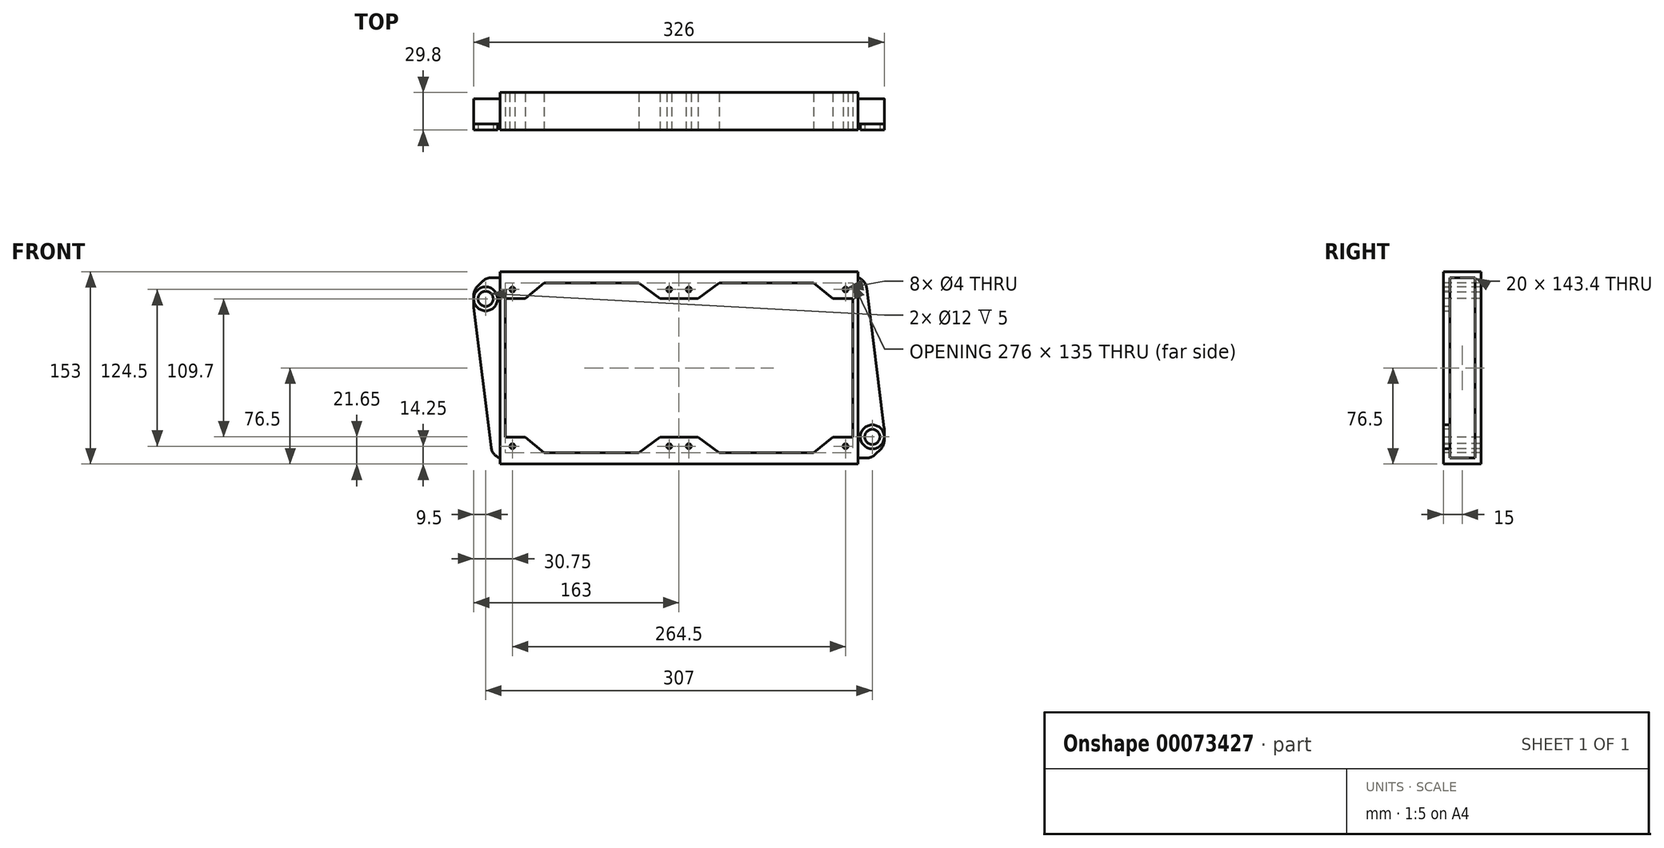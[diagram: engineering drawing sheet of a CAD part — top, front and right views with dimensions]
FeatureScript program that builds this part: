
annotation { "Feature Type Name" : "Feature", "Feature Type Description" : "" }
export const myFeature = defineFeature(function(context is Context, id is Id, definition is map)
    precondition{}
    {
        {
            var Q0;
            Q0=qCreatedBy(makeId("Front.planeOp"),FACE);
            var sketch = newSketch(context, id + "F0", { "sketchPlane" : qUnion([Q0])});
            skLineSegment(sketch, "E0.bottom", {"start": v(0, 71.7) * mm, "end": v(326, 71.7) * mm});
            skLineSegment(sketch, "E0.top", {"start": v(0, -71.7) * mm, "end": v(326, -71.7) * mm});
            skLineSegment(sketch, "E0.left", {"start": v(0, 71.7) * mm, "end": v(0, -71.7) * mm});
            skLineSegment(sketch, "E0.right", {"start": v(326, 71.7) * mm, "end": v(326, -71.7) * mm});
            skPoint(sketch, "E1", {"position": v(0, 0) * mm});
            skSolve(sketch);
        }
        {
            var Q0;
            Q0=qSketchRegion(id+"F0",true);
            extrude(context, id + "F1", {"entities" : qUnion([Q0]), "depth" : 20 * mm});
        }
        {
            var Q0;
            Q0=makeQuery(id+"F1.opExtrude","CAP_FACE",FACE,{"disambiguationData":[OSD([sQuery(id+"F0.wireOp",EDGE,"E0.bottom"),sQuery(id+"F0.wireOp",EDGE,"E0.top"),sQuery(id+"F0.wireOp",EDGE,"E0.left"),sQuery(id+"F0.wireOp",EDGE,"E0.right")])],"isStart":false});
            var sketch = newSketch(context, id + "F2", { "sketchPlane" : qUnion([Q0])});
            skCircle(sketch, "E2", {"center": v(9.5, 54.85) * mm, "radius": 9.5 * mm});
            skCircle(sketch, "E3", {"center": v(316.5, -54.85) * mm, "radius": 9.5 * mm});
            skLineSegment(sketch, "E4", {"start": v(326, 0) * mm, "end": v(0, 0) * mm, "construction": true});
            skSolve(sketch);
        }
        {
            var Q0;
            Q0=qSketchRegion(id+"F2",true);
            extrude(context, id + "F3", {"entities" : qUnion([Q0]), "operationType" : NewBodyOperationType.ADD, "depth" : 5 * mm});
        }
        {
            var Q0;
            Q0=makeQuery(id+"F3.opExtrude","CAP_FACE",FACE,{"disambiguationData":[OSD([sQuery(id+"F2.wireOp",EDGE,"E2")])],"isStart":false});
            var sketch = newSketch(context, id + "F4", { "sketchPlane" : qUnion([Q0])});
            skCircle(sketch, "E5", {"center": v(9.5, 54.85) * mm, "radius": 6 * mm});
            skCircle(sketch, "E6", {"center": v(316.5, -54.85) * mm, "radius": 6 * mm});
            skSolve(sketch);
        }
        {
            var Q0;
            Q0=qSketchRegion(id+"F4",true);
            extrude(context, id + "F5", {"entities" : qUnion([Q0]), "operationType" : NewBodyOperationType.REMOVE, "oppositeDirection" : true, "depth" : 5 * mm});
        }
        {
            var Q0;
            Q0=makeQuery(id+"F1.opExtrude","SWEPT_FACE",FACE,{"disambiguationData":[OSD([sQuery(id+"F0.wireOp",EDGE,"E0.left")])]});
            cPlane(context, id + "F6", {"entities" : qUnion([Q0]), "cplaneType" : CPlaneType.OFFSET, "offset" : 21 * mm, "oppositeDirection" : true, "width" : 150 * mm, "height" : 150 * mm});
        }
        {
            var Q0;
            Q0=qCreatedBy(id+"F6.planeOp",FACE);
            var sketch = newSketch(context, id + "F7", { "sketchPlane" : qUnion([Q0])});
            skLineSegment(sketch, "E7.bottom", {"start": v(-4.8, 76.5) * mm, "end": v(24.8, 76.5) * mm});
            skLineSegment(sketch, "E7.top", {"start": v(-4.8, -76.5) * mm, "end": v(24.8, -76.5) * mm});
            skLineSegment(sketch, "E7.left", {"start": v(-4.8, 76.5) * mm, "end": v(-4.8, -76.5) * mm});
            skLineSegment(sketch, "E7.right", {"start": v(24.8, 76.5) * mm, "end": v(24.8, -76.5) * mm});
            skLineSegment(sketch, "E8", {"start": v(0, 0) * mm, "end": v(-4.8, 0) * mm, "construction": true});
            skLineSegment(sketch, "E9.bottom", {"start": v(0, 71.7) * mm, "end": v(20, 71.7) * mm});
            skLineSegment(sketch, "E9.top", {"start": v(0, -71.7) * mm, "end": v(20, -71.7) * mm});
            skLineSegment(sketch, "E9.left", {"start": v(0, 71.7) * mm, "end": v(0, -71.7) * mm});
            skLineSegment(sketch, "E9.right", {"start": v(20, 71.7) * mm, "end": v(20, -71.7) * mm});
            skSolve(sketch);
        }
        {
            var Q0;
            Q0=qSketchRegion(id+"F7",true);
            extrude(context, id + "F8", {"entities" : qUnion([Q0]), "oppositeDirection" : true, "depth" : 284 * mm});
        }
        {
            var Q0;
            Q0=makeQuery(id+"F8.opExtrude","SWEPT_FACE",FACE,{"disambiguationData":[OSD([sQuery(id+"F7.wireOp",EDGE,"E7.right")])]});
            var sketch = newSketch(context, id + "F9", { "sketchPlane" : qUnion([Q0])});
            skCircle(sketch, "E10", {"center": v(30.75, 62.25) * mm, "radius": 2 * mm});
            skCircle(sketch, "E11", {"center": v(155.25, 62.25) * mm, "radius": 2 * mm});
            skCircle(sketch, "E12", {"center": v(170.75, 62.25) * mm, "radius": 2 * mm});
            skCircle(sketch, "E13", {"center": v(295.25, 62.25) * mm, "radius": 2 * mm});
            skLineSegment(sketch, "E14", {"start": v(21, 0) * mm, "end": v(305, 0) * mm, "construction": true});
            skLineSegment(sketch, "E15", {"start": v(163, 76.5) * mm, "end": v(163, -76.5) * mm, "construction": true});
            skCircle(sketch, "E16.MirrorC", {"center": v(30.75, -62.25) * mm, "radius": 2 * mm});
            skCircle(sketch, "E17.MirrorC", {"center": v(155.25, -62.25) * mm, "radius": 2 * mm});
            skCircle(sketch, "E18.MirrorC", {"center": v(170.75, -62.25) * mm, "radius": 2 * mm});
            skCircle(sketch, "E19.MirrorC", {"center": v(295.25, -62.25) * mm, "radius": 2 * mm});
            skSolve(sketch);
        }
        {
            var Q0;
            Q0=qSketchRegion(id+"F9",true);
            extrude(context, id + "F10", {"entities" : qUnion([Q0]), "operationType" : NewBodyOperationType.REMOVE, "endBound" : BoundingType.THROUGH_ALL, "oppositeDirection" : true, "depth" : 25 * mm});
        }
        {
            var Q0;
            Q0=makeQuery(id+"F8.opExtrude","SWEPT_FACE",FACE,{"disambiguationData":[OSD([sQuery(id+"F7.wireOp",EDGE,"E7.right")])]});
            var sketch = newSketch(context, id + "F11", { "sketchPlane" : qUnion([Q0])});
            skLineSegment(sketch, "E20", {"start": v(21, 55) * mm, "end": v(25, 55) * mm, "construction": true});
            skLineSegment(sketch, "E21", {"start": v(41, 55) * mm, "end": v(56, 67.5) * mm});
            skLineSegment(sketch, "E22", {"start": v(56, 67.5) * mm, "end": v(131, 67.5) * mm});
            skLineSegment(sketch, "E23", {"start": v(131, 67.5) * mm, "end": v(148, 55) * mm});
            skLineSegment(sketch, "E24", {"start": v(148, 55) * mm, "end": v(178, 55) * mm});
            skLineSegment(sketch, "E25", {"start": v(178, 55) * mm, "end": v(195, 67.5) * mm});
            skLineSegment(sketch, "E26", {"start": v(195, 67.5) * mm, "end": v(270, 67.5) * mm});
            skLineSegment(sketch, "E27", {"start": v(270, 67.5) * mm, "end": v(285, 55) * mm});
            skLineSegment(sketch, "E28", {"start": v(285, 55) * mm, "end": v(301, 55) * mm});
            skLineSegment(sketch, "E29", {"start": v(305, 55) * mm, "end": v(305, 0) * mm, "construction": true});
            skLineSegment(sketch, "E30", {"start": v(21, 55) * mm, "end": v(21, 0) * mm, "construction": true});
            skLineSegment(sketch, "E31", {"start": v(21, 0) * mm, "end": v(305, 0) * mm, "construction": true});
            skLineSegment(sketch, "E32", {"start": v(163, 76.5) * mm, "end": v(163, 55) * mm, "construction": true});
            skLineSegment(sketch, "E33.MirrorCS", {"start": v(305, -55) * mm, "end": v(305, 0) * mm, "construction": true});
            skLineSegment(sketch, "E34.MirrorCS", {"start": v(285, -55) * mm, "end": v(301, -55) * mm});
            skLineSegment(sketch, "E35.MirrorCS", {"start": v(270, -67.5) * mm, "end": v(285, -55) * mm});
            skLineSegment(sketch, "E36.MirrorCS", {"start": v(195, -67.5) * mm, "end": v(270, -67.5) * mm});
            skLineSegment(sketch, "E37.MirrorCS", {"start": v(178, -55) * mm, "end": v(195, -67.5) * mm});
            skLineSegment(sketch, "E38.MirrorCS", {"start": v(148, -55) * mm, "end": v(178, -55) * mm});
            skLineSegment(sketch, "E39.MirrorCS", {"start": v(131, -67.5) * mm, "end": v(148, -55) * mm});
            skLineSegment(sketch, "E40.MirrorCS", {"start": v(56, -67.5) * mm, "end": v(131, -67.5) * mm});
            skLineSegment(sketch, "E41.MirrorCS", {"start": v(41, -55) * mm, "end": v(56, -67.5) * mm});
            skLineSegment(sketch, "E42.MirrorCS", {"start": v(21, -55) * mm, "end": v(21, 0) * mm, "construction": true});
            skLineSegment(sketch, "E43.MirrorCS", {"start": v(21, -55) * mm, "end": v(25, -55) * mm, "construction": true});
            skLineSegment(sketch, "E44", {"start": v(25, 55) * mm, "end": v(25, -55) * mm});
            skLineSegment(sketch, "E45", {"start": v(301, 55) * mm, "end": v(301, -55) * mm});
            skLineSegment(sketch, "E46", {"start": v(301, 55) * mm, "end": v(305, 55) * mm, "construction": true});
            skLineSegment(sketch, "E47", {"start": v(301, -55) * mm, "end": v(305, -55) * mm, "construction": true});
            skLineSegment(sketch, "E48", {"start": v(25, -55) * mm, "end": v(41, -55) * mm});
            skLineSegment(sketch, "E49", {"start": v(25, 55) * mm, "end": v(41, 55) * mm});
            skSolve(sketch);
        }
        {
            var Q0;
            Q0=qSketchRegion(id+"F11",true);
            extrude(context, id + "F12", {"entities" : qUnion([Q0]), "operationType" : NewBodyOperationType.REMOVE, "endBound" : BoundingType.THROUGH_ALL, "oppositeDirection" : true, "depth" : 25 * mm});
        }
        {
            var Q0;
            Q0=makeQuery(id+"F1.opExtrude","SWEPT_BODY",BODY,{"disambiguationData":[OSD([sQuery(id+"F0.wireOp",EDGE,"E0.bottom"),sQuery(id+"F0.wireOp",EDGE,"E0.top"),sQuery(id+"F0.wireOp",EDGE,"E0.left"),sQuery(id+"F0.wireOp",EDGE,"E0.right")])]});
            var Q1;
            Q1=makeQuery(id+"F8.opExtrude","SWEPT_BODY",BODY,{"disambiguationData":[OSD([sQuery(id+"F7.wireOp",EDGE,"E7.bottom"),sQuery(id+"F7.wireOp",EDGE,"E7.top"),sQuery(id+"F7.wireOp",EDGE,"E7.left"),sQuery(id+"F7.wireOp",EDGE,"E7.right"),sQuery(id+"F7.wireOp",EDGE,"E9.bottom"),sQuery(id+"F7.wireOp",EDGE,"E9.top"),sQuery(id+"F7.wireOp",EDGE,"E9.left"),sQuery(id+"F7.wireOp",EDGE,"E9.right")])]});
            var Q2;
            Q2=makeQuery(id+"F8.opExtrude","SWEPT_BODY",BODY,{"disambiguationData":[OSD([sQuery(id+"F7.wireOp",EDGE,"E7.bottom"),sQuery(id+"F7.wireOp",EDGE,"E7.top"),sQuery(id+"F7.wireOp",EDGE,"E7.left"),sQuery(id+"F7.wireOp",EDGE,"E7.right"),sQuery(id+"F7.wireOp",EDGE,"E9.bottom"),sQuery(id+"F7.wireOp",EDGE,"E9.top"),sQuery(id+"F7.wireOp",EDGE,"E9.left"),sQuery(id+"F7.wireOp",EDGE,"E9.right")])]});
            booleanBodies(context, id + "F13", {"operationType" : BooleanOperationType.UNION, "tools" : qUnion([Q0, Q1, Q2])});
        }
        {
            var Q0;
            Q0=makeQuery(id+"F1.opExtrude","SWEPT_EDGE",EDGE,{"disambiguationData":[OSD([sQuery(id+"F0.wireOp",EDGE,"E0.top"),sQuery(id+"F0.wireOp",EDGE,"E0.left")])]});
            var Q1;
            Q1=makeQuery(id+"F1.opExtrude","SWEPT_EDGE",EDGE,{"disambiguationData":[OSD([sQuery(id+"F0.wireOp",EDGE,"E0.bottom"),sQuery(id+"F0.wireOp",EDGE,"E0.right")])]});
            chamfer(context, id + "F14", {"entities" : qUnion([Q0, Q1]), "chamferType" : ChamferType.TWO_OFFSETS, "width1" : 15 * mm, "oppositeDirection" : false, "width2" : 120 * mm, "tangentPropagation" : true});
        }
        {
            var Q0;
            Q0=makeQuery(id+"F1.opExtrude","SWEPT_EDGE",EDGE,{"disambiguationData":[OSD([sQuery(id+"F0.wireOp",EDGE,"E0.bottom"),sQuery(id+"F0.wireOp",EDGE,"E0.left")])]});
            var Q1;
            Q1=makeQuery(id+"F1.opExtrude","SWEPT_EDGE",EDGE,{"disambiguationData":[OSD([sQuery(id+"F0.wireOp",EDGE,"E0.top"),sQuery(id+"F0.wireOp",EDGE,"E0.right")])]});
            chamfer(context, id + "F15", {"entities" : qUnion([Q0, Q1]), "width" : 10 * mm, "tangentPropagation" : true});
        }
        {
            var Q0;
            {var subQ1=sQuery(id+"F0.wireOp",EDGE,"E0.left");var subQ3=sQuery(id+"F0.wireOp",EDGE,"E0.bottom");Q0=makeQuery(id+"F15.opChamfer","BLEND_EDGE",EDGE,{"blendedFrom":[makeQuery(id+"F1.opExtrude","SWEPT_EDGE",EDGE,{"disambiguationData":[OSD([subQ3,subQ1])]}),makeQuery(id+"F13.opBoolean","SPLIT",FACE,{"disambiguationData":[TD([makeQuery(id+"F1.opExtrude","SWEPT_FACE",FACE,{"disambiguationData":[OSD([subQ1])]})])],"derivedFrom":makeQuery(id+"F1.opExtrude","SWEPT_FACE",FACE,{"disambiguationData":[OSD([subQ3])]})})],"blendedInto":[makeQuery(id+"F13.opBoolean","SPLIT",FACE,{"disambiguationData":[TD([makeQuery(id+"F1.opExtrude","SWEPT_FACE",FACE,{"disambiguationData":[OSD([subQ1])]})])],"derivedFrom":makeQuery(id+"F1.opExtrude","SWEPT_FACE",FACE,{"disambiguationData":[OSD([subQ3])]})})]});}
            var Q1;
            {var subQ0=sQuery(id+"F0.wireOp",EDGE,"E0.left");Q1=makeQuery(id+"F15.opChamfer","BLEND_EDGE",EDGE,{"blendedFrom":[makeQuery(id+"F1.opExtrude","SWEPT_EDGE",EDGE,{"disambiguationData":[OSD([sQuery(id+"F0.wireOp",EDGE,"E0.bottom"),subQ0])]}),makeQuery(id+"F1.opExtrude","SWEPT_FACE",FACE,{"disambiguationData":[OSD([subQ0])]})],"blendedInto":[makeQuery(id+"F1.opExtrude","SWEPT_FACE",FACE,{"disambiguationData":[OSD([subQ0])]})]});}
            var Q2;
            {var subQ0=sQuery(id+"F0.wireOp",EDGE,"E0.left");Q2=makeQuery(id+"F14.opChamfer","BLEND_EDGE",EDGE,{"blendedFrom":[makeQuery(id+"F1.opExtrude","SWEPT_EDGE",EDGE,{"disambiguationData":[OSD([sQuery(id+"F0.wireOp",EDGE,"E0.top"),subQ0])]}),makeQuery(id+"F1.opExtrude","SWEPT_FACE",FACE,{"disambiguationData":[OSD([subQ0])]})],"blendedInto":[makeQuery(id+"F1.opExtrude","SWEPT_FACE",FACE,{"disambiguationData":[OSD([subQ0])]})]});}
            var Q3;
            {var subQ1=sQuery(id+"F0.wireOp",EDGE,"E0.left");var subQ2=sQuery(id+"F0.wireOp",EDGE,"E0.top");Q3=makeQuery(id+"F14.opChamfer","BLEND_EDGE",EDGE,{"blendedFrom":[makeQuery(id+"F1.opExtrude","SWEPT_EDGE",EDGE,{"disambiguationData":[OSD([subQ2,subQ1])]}),makeQuery(id+"F13.opBoolean","SPLIT",FACE,{"disambiguationData":[TD([makeQuery(id+"F1.opExtrude","SWEPT_FACE",FACE,{"disambiguationData":[OSD([subQ1])]})])],"derivedFrom":makeQuery(id+"F1.opExtrude","SWEPT_FACE",FACE,{"disambiguationData":[OSD([subQ2])]})})],"blendedInto":[makeQuery(id+"F13.opBoolean","SPLIT",FACE,{"disambiguationData":[TD([makeQuery(id+"F1.opExtrude","SWEPT_FACE",FACE,{"disambiguationData":[OSD([subQ1])]})])],"derivedFrom":makeQuery(id+"F1.opExtrude","SWEPT_FACE",FACE,{"disambiguationData":[OSD([subQ2])]})})]});}
            var Q4;
            {var subQ0=sQuery(id+"F0.wireOp",EDGE,"E0.right");var subQ2=sQuery(id+"F0.wireOp",EDGE,"E0.top");Q4=makeQuery(id+"F15.opChamfer","BLEND_EDGE",EDGE,{"blendedFrom":[makeQuery(id+"F1.opExtrude","SWEPT_EDGE",EDGE,{"disambiguationData":[OSD([subQ2,subQ0])]}),makeQuery(id+"F13.opBoolean","SPLIT",FACE,{"disambiguationData":[TD([makeQuery(id+"F1.opExtrude","SWEPT_FACE",FACE,{"disambiguationData":[OSD([subQ0])]})])],"derivedFrom":makeQuery(id+"F1.opExtrude","SWEPT_FACE",FACE,{"disambiguationData":[OSD([subQ2])]})})],"blendedInto":[makeQuery(id+"F13.opBoolean","SPLIT",FACE,{"disambiguationData":[TD([makeQuery(id+"F1.opExtrude","SWEPT_FACE",FACE,{"disambiguationData":[OSD([subQ0])]})])],"derivedFrom":makeQuery(id+"F1.opExtrude","SWEPT_FACE",FACE,{"disambiguationData":[OSD([subQ2])]})})]});}
            var Q5;
            {var subQ0=sQuery(id+"F0.wireOp",EDGE,"E0.right");Q5=makeQuery(id+"F15.opChamfer","BLEND_EDGE",EDGE,{"blendedFrom":[makeQuery(id+"F1.opExtrude","SWEPT_EDGE",EDGE,{"disambiguationData":[OSD([sQuery(id+"F0.wireOp",EDGE,"E0.top"),subQ0])]}),makeQuery(id+"F1.opExtrude","SWEPT_FACE",FACE,{"disambiguationData":[OSD([subQ0])]})],"blendedInto":[makeQuery(id+"F1.opExtrude","SWEPT_FACE",FACE,{"disambiguationData":[OSD([subQ0])]})]});}
            var Q6;
            {var subQ0=sQuery(id+"F0.wireOp",EDGE,"E0.right");Q6=makeQuery(id+"F14.opChamfer","BLEND_EDGE",EDGE,{"blendedFrom":[makeQuery(id+"F1.opExtrude","SWEPT_EDGE",EDGE,{"disambiguationData":[OSD([sQuery(id+"F0.wireOp",EDGE,"E0.bottom"),subQ0])]}),makeQuery(id+"F1.opExtrude","SWEPT_FACE",FACE,{"disambiguationData":[OSD([subQ0])]})],"blendedInto":[makeQuery(id+"F1.opExtrude","SWEPT_FACE",FACE,{"disambiguationData":[OSD([subQ0])]})]});}
            var Q7;
            {var subQ0=sQuery(id+"F0.wireOp",EDGE,"E0.right");var subQ3=sQuery(id+"F0.wireOp",EDGE,"E0.bottom");Q7=makeQuery(id+"F14.opChamfer","BLEND_EDGE",EDGE,{"blendedFrom":[makeQuery(id+"F1.opExtrude","SWEPT_EDGE",EDGE,{"disambiguationData":[OSD([subQ3,subQ0])]}),makeQuery(id+"F13.opBoolean","SPLIT",FACE,{"disambiguationData":[TD([makeQuery(id+"F1.opExtrude","SWEPT_FACE",FACE,{"disambiguationData":[OSD([subQ0])]})])],"derivedFrom":makeQuery(id+"F1.opExtrude","SWEPT_FACE",FACE,{"disambiguationData":[OSD([subQ3])]})})],"blendedInto":[makeQuery(id+"F13.opBoolean","SPLIT",FACE,{"disambiguationData":[TD([makeQuery(id+"F1.opExtrude","SWEPT_FACE",FACE,{"disambiguationData":[OSD([subQ0])]})])],"derivedFrom":makeQuery(id+"F1.opExtrude","SWEPT_FACE",FACE,{"disambiguationData":[OSD([subQ3])]})})]});}
            fillet(context, id + "F16", {"entities" : qUnion([Q0, Q1, Q2, Q3, Q4, Q5, Q6, Q7]), "radius" : 10 * mm, "tangentPropagation" : true, "allowEdgeOverflow" : false});
        }
    });
